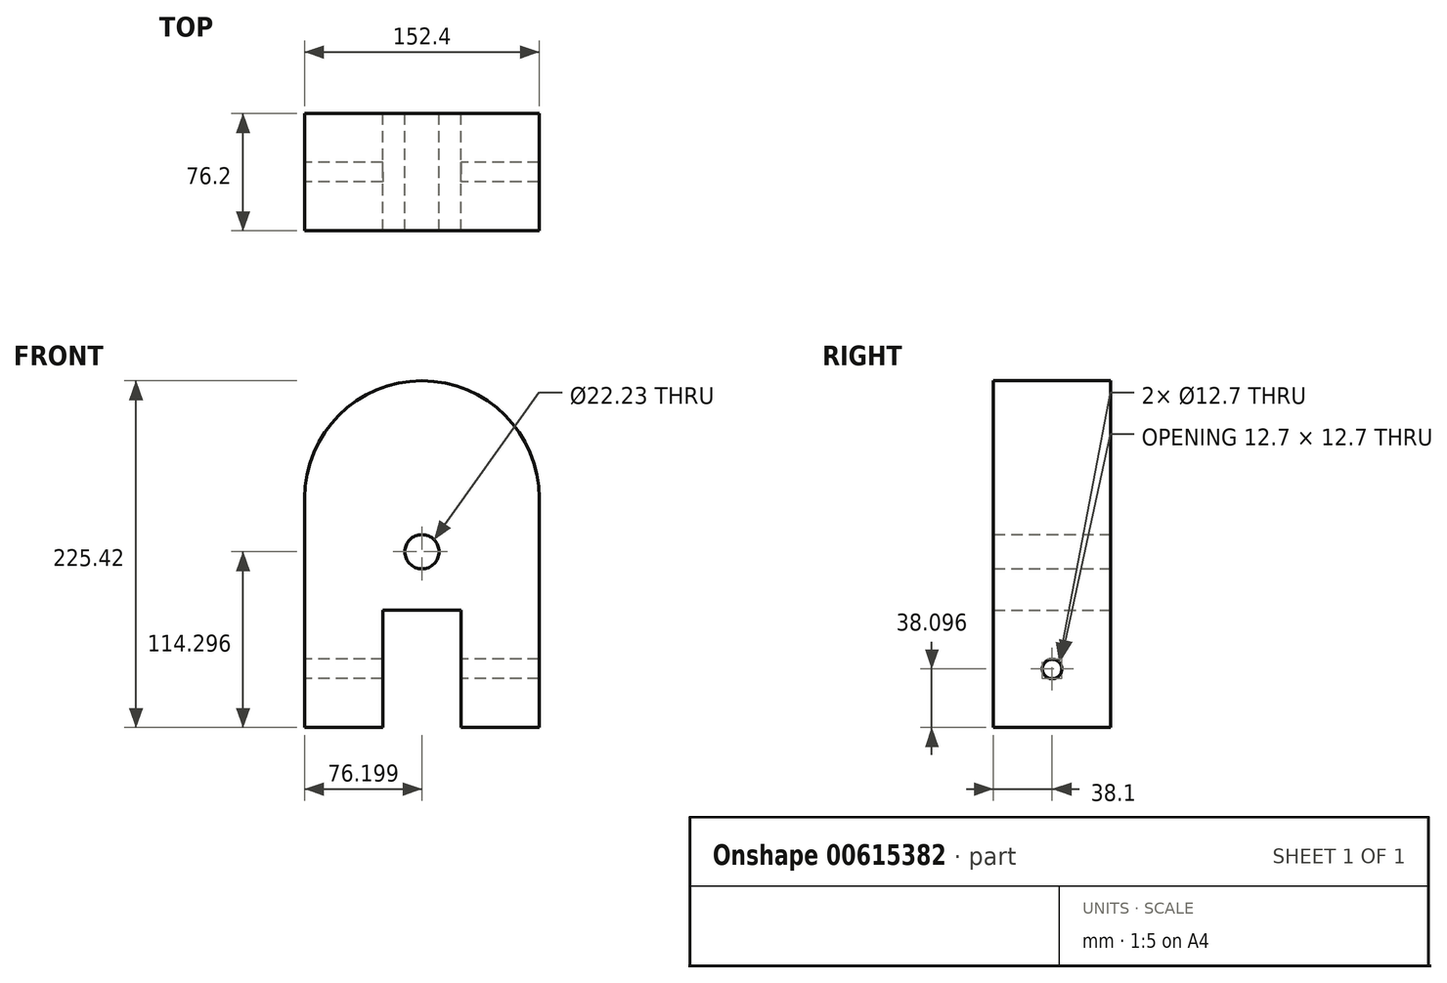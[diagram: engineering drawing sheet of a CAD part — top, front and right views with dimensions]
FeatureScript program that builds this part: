
annotation { "Feature Type Name" : "Feature", "Feature Type Description" : "" }
export const myFeature = defineFeature(function(context is Context, id is Id, definition is map)
    precondition{}
    {
        {
            var Q0;
            Q0=qCreatedBy(makeId("Front.planeOp"),FACE);
            var sketch = newSketch(context, id + "F0", { "sketchPlane" : qUnion([Q0])});
            skLineSegment(sketch, "E0", {"start": v(-99.16, -42.41) * mm, "end": v(-99.16, 106.81) * mm});
            skLineSegment(sketch, "E1", {"start": v(-22.96, 183.01) * mm, "end": v(-22.96, 183.01) * mm});
            skLineSegment(sketch, "E2", {"start": v(53.24, 106.81) * mm, "end": v(53.24, -42.41) * mm});
            skLineSegment(sketch, "E3", {"start": v(53.24, -42.41) * mm, "end": v(2.44, -42.41) * mm});
            skLineSegment(sketch, "E4", {"start": v(2.44, -42.41) * mm, "end": v(2.44, 33.79) * mm});
            skLineSegment(sketch, "E5", {"start": v(2.44, 33.79) * mm, "end": v(-48.36, 33.79) * mm});
            skLineSegment(sketch, "E6", {"start": v(-48.36, 33.79) * mm, "end": v(-48.36, -42.41) * mm});
            skLineSegment(sketch, "E7", {"start": v(-48.36, -42.41) * mm, "end": v(-99.16, -42.41) * mm});
            skPoint(sketch, "E8.visualSharp", {"position": v(-99.16, 183.01) * mm});
            skArc(sketch, "E8.filletArc", {"start": v(-22.96, 183.01) * mm, "mid": v(-76.84, 160.7) * mm, "end": v(-99.16, 106.81) * mm});
            skPoint(sketch, "E9.visualSharp", {"position": v(53.24, 183.01) * mm});
            skArc(sketch, "E9.filletArc", {"start": v(53.24, 106.81) * mm, "mid": v(30.92, 160.7) * mm, "end": v(-22.96, 183.01) * mm});
            skCircle(sketch, "E10", {"center": v(-22.96, 71.89) * mm, "radius": 11.11 * mm});
            skSolve(sketch);
        }
        {
            var Q0;
            Q0 = qSketchRegion(id + "F0", true);
            extrude(context, id + "F1", {"entities" : qUnion([Q0]), "depth" : 76.2 * mm, "offsetDistance" : 25.4 * mm});
        }
        {
            var Q0;
            Q0=makeQuery(id+"F1.opExtrude","SWEPT_FACE",FACE,{"disambiguationData":[OSD([sQuery(id+"F0.wireOp",EDGE,"E0")])]});
            cPlane(context, id + "F2", {"entities" : qUnion([Q0]), "cplaneType" : CPlaneType.OFFSET, "offset" : 0 * mm, "width" : 152.4 * mm, "height" : 152.4 * mm});
        }
        {
            var Q0;
            Q0=qCreatedBy(id+"F2.planeOp",FACE);
            var sketch = newSketch(context, id + "F3", { "sketchPlane" : qUnion([Q0])});
            skCircle(sketch, "E11", {"center": v(38.1, -4.31) * mm, "radius": 6.35 * mm});
            skSolve(sketch);
        }
        {
            var Q0;
            Q0 = qSketchRegion(id + "F3", true);
            extrude(context, id + "F4", {"entities" : qUnion([Q0]), "operationType" : NewBodyOperationType.REMOVE, "oppositeDirection" : true, "depth" : 254 * mm, "offsetDistance" : 25.4 * mm});
        }
    });
